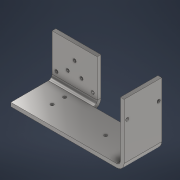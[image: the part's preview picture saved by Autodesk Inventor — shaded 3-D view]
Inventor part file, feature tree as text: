
AUTODESK INVENTOR PART (.ipt)
format: ipt  version: 2021 (Build 250183000, 183)  size: 218,624 bytes
history: native  units: mm
features: sheet_metal_op x9, sketch x7, other x4, hole x3, mirror x1, plane x1, split x1
ambient origin geometry x8: Origin, YZ Plane, XZ Plane, XY Plane, X Axis, Y Axis, Z Axis, Center Point
bodies: Solid1 (feature_tree)
feature tree (26):
  sheet_metal_op  "Face1"
  sheet_metal_op  "Flange1"
  sheet_metal_op  "Face2"
  sheet_metal_op  "Flange2"
  hole  "Hole1"  [1 undecoded]
  hole  "Hole2"  [1 undecoded]
  hole  "Hole3"  [1 undecoded]
  mirror  "Mirror1"
  plane  "Work Plane1"
  split  "Split1"
  sketch  "Sketch1"  dims[d0=72.0mm d1=36.0mm]
  other  "Plate1"
  sketch  "Sketch2"  dims[d2=72.0mm d3=36.0mm]
  other  "Plate2"
  sheet_metal_op  "Bend1"
  sheet_metal_op  "Corner1"
  sketch  "Sketch3"  dims[d4=6.0mm d5=6.0mm]
  other  "Plate3"
  sheet_metal_op  "Bend2"
  sketch  "Sketch4"  dims[d6=3.0mm]
  other  "Plate4"
  sheet_metal_op  "Bend3"
  sheet_metal_op  "Corner2"
  sketch  "Sketch5"  dims[d7=12.0mm]
  sketch  "Sketch6"  dims[d8=6.0mm]
  sketch  "Sketch7"  dims[d9=72.0mm d10=90.0deg d11=6.0mm d12=24.0mm d13=6.0mm d14=6.0mm d15=109.0mm d16=60.0mm d17=6.0mm d18=6.0mm d19=3.0mm d20=12.0mm d21=6.0mm d22=6.0mm d23=3.0mm d24=12.0mm d25=6.0mm d26=100.6mm d27=90.0deg d28=6.0mm d29=24.0mm d30=6.0mm d31=6.0mm d32=60.0mm d33=30.0mm d34=30.0mm d35=50.0mm d36=30.0mm d37=30.0mm d38=5.0mm d39=6.0mm d40=4.0mm d41=2.0mm d42=90.0deg d43=6.0mm d44=0.0mm d45=36.0mm d46=25.4mm d47=67.0mm d48=120.0deg d49=120.0deg d50=0.0mm d51=5.0mm d52=6.0mm d53=4.0mm d54=2.0mm d55=90.0deg d56=6.0mm d57=0.0mm d58=5.0mm d59=6.0mm d60=4.0mm d61=2.0mm d62=90.0deg d63=6.0mm d64=0.0mm d65=60.0mm d66=72.0mm d67=30.0mm d68=30.0mm d69=36.0mm d70=20.0mm d71=10.0mm d72=36.0mm d73=99.040396mm d74=49.520198mm]
note: 3 required parameter values undecoded (feature->parameter linkage not recoverable at this tier; creation-order binding heuristic only, values carry confidence <= 0.55)
